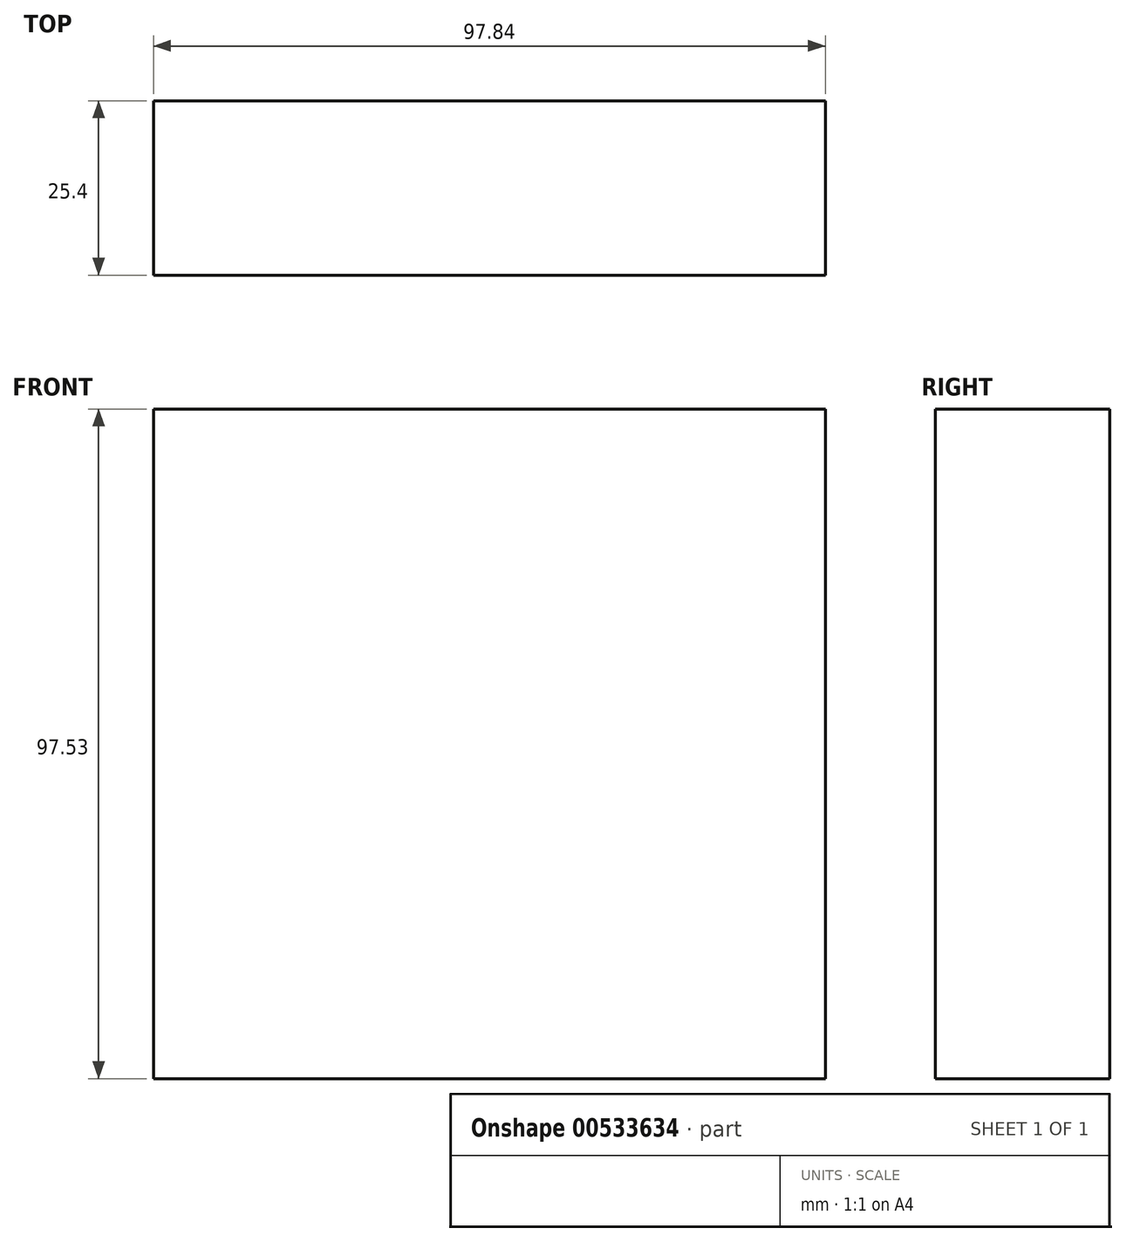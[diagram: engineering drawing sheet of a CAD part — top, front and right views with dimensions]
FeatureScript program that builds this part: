
annotation { "Feature Type Name" : "Feature", "Feature Type Description" : "" }
export const myFeature = defineFeature(function(context is Context, id is Id, definition is map)
    precondition{}
    {
        {
            var Q0;
            Q0=qCreatedBy(makeId("Front.planeOp"),FACE);
            var sketch = newSketch(context, id + "F0", { "sketchPlane" : qUnion([Q0])});
            skLineSegment(sketch, "E0.bottom", {"start": v(-47.55, 44.04) * mm, "end": v(50.3, 44.04) * mm});
            skLineSegment(sketch, "E0.top", {"start": v(-47.55, -53.5) * mm, "end": v(50.3, -53.5) * mm});
            skLineSegment(sketch, "E0.left", {"start": v(-47.55, 44.04) * mm, "end": v(-47.55, -53.5) * mm});
            skLineSegment(sketch, "E0.right", {"start": v(50.3, 44.04) * mm, "end": v(50.3, -53.5) * mm});
            skLineSegment(sketch, "E1", {"start": v(5.49, 44.04) * mm, "end": v(5.49, -55.93) * mm});
            skLineSegment(sketch, "E2", {"start": v(-47.55, -4.72) * mm, "end": v(50.3, -4.72) * mm});
            skSolve(sketch);
        }
        {
            var Q0;
            {var subQ0=sQuery(id+"F0.wireOp",EDGE,"E0.left");var subQ1=sQuery(id+"F0.wireOp",EDGE,"E0.bottom");var subQ2=makeQuery(id+"F0.imprint","INTERSECT",VERTEX,{"derivedFrom":[subQ1,subQ0]});Q0=makeQuery(id+"F0.imprint","IMPRINT",FACE,{"disambiguationData":[TD([[makeQuery(id+"F0.imprint","IMPRINT",EDGE,{"disambiguationData":[TD([[subQ2,-1.0]])],"derivedFrom":subQ1}),-1.0]])]});}
            var Q1;
            {var subQ0=sQuery(id+"F0.wireOp",EDGE,"E0.right");var subQ1=sQuery(id+"F0.wireOp",EDGE,"E0.bottom");var subQ2=makeQuery(id+"F0.imprint","INTERSECT",VERTEX,{"derivedFrom":[subQ1,subQ0]});Q1=makeQuery(id+"F0.imprint","IMPRINT",FACE,{"disambiguationData":[TD([[makeQuery(id+"F0.imprint","IMPRINT",EDGE,{"disambiguationData":[TD([[subQ2,1.0]])],"derivedFrom":subQ1}),-1.0]])]});}
            var Q2;
            {var subQ0=sQuery(id+"F0.wireOp",EDGE,"E0.right");var subQ1=sQuery(id+"F0.wireOp",EDGE,"E0.top");var subQ2=makeQuery(id+"F0.imprint","INTERSECT",VERTEX,{"derivedFrom":[subQ1,subQ0]});Q2=makeQuery(id+"F0.imprint","IMPRINT",FACE,{"disambiguationData":[TD([[makeQuery(id+"F0.imprint","IMPRINT",EDGE,{"disambiguationData":[TD([[subQ2,1.0]])],"derivedFrom":subQ1}),1.0]])]});}
            var Q3;
            {var subQ0=sQuery(id+"F0.wireOp",EDGE,"E0.left");var subQ1=sQuery(id+"F0.wireOp",EDGE,"E0.top");var subQ2=makeQuery(id+"F0.imprint","INTERSECT",VERTEX,{"derivedFrom":[subQ1,subQ0]});Q3=makeQuery(id+"F0.imprint","IMPRINT",FACE,{"disambiguationData":[TD([[makeQuery(id+"F0.imprint","IMPRINT",EDGE,{"disambiguationData":[TD([[subQ2,-1.0]])],"derivedFrom":subQ1}),1.0]])]});}
            extrude(context, id + "F1", {"entities" : qUnion([Q0, Q1, Q2, Q3]), "depth" : 25.4 * mm, "offsetDistance" : 25.4 * mm});
        }
    });
